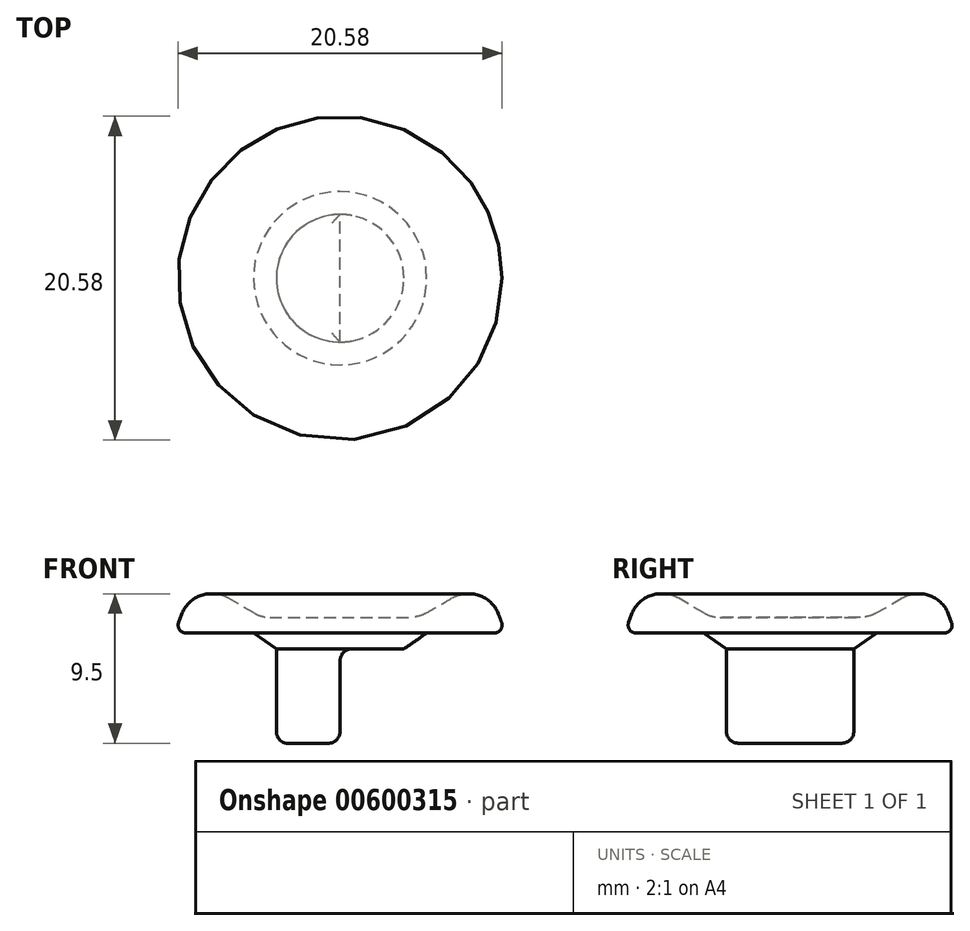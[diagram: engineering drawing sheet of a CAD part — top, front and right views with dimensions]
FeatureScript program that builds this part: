
annotation { "Feature Type Name" : "Feature", "Feature Type Description" : "" }
export const myFeature = defineFeature(function(context is Context, id is Id, definition is map)
    precondition{}
    {
        {
            var Q0;
            Q0=qCreatedBy(makeId("Front.planeOp"),FACE);
            var sketch = newSketch(context, id + "F0", { "sketchPlane" : qUnion([Q0])});
            skLineSegment(sketch, "E0", {"start": v(4.05, 6) * mm, "end": v(5.5, 7) * mm});
            skLineSegment(sketch, "E1", {"start": v(5.5, 7) * mm, "end": v(10.5, 7) * mm});
            skLineSegment(sketch, "E2", {"start": v(0, 8) * mm, "end": v(0, 0) * mm});
            skLineSegment(sketch, "E3", {"start": v(4.05, 6) * mm, "end": v(4.05, 0) * mm});
            skLineSegment(sketch, "E4", {"start": v(4.05, 0) * mm, "end": v(0, 0) * mm});
            skPoint(sketch, "E5.orphan", {"position": v(0, 0) * mm});
            skLineSegment(sketch, "E6", {"start": v(10.5, 7) * mm, "end": v(9.6, 9.5) * mm});
            skLineSegment(sketch, "E7", {"start": v(9.6, 9.5) * mm, "end": v(7.6, 9.5) * mm});
            skLineSegment(sketch, "E8", {"start": v(7.6, 9.5) * mm, "end": v(5, 8) * mm});
            skLineSegment(sketch, "E9", {"start": v(5, 8) * mm, "end": v(0, 8) * mm});
            skSolve(sketch);
        }
        {
            var Q0;
            Q0=qSketchRegion(id+"F0",true);
            var Q1;
            Q1=sQuery(id+"F0.wireOp",EDGE,"E2");
            revolve(context, id + "F1", {"entities" : qUnion([Q0]), "axis" : qUnion([Q1]), "revolveType" : RevolveType.FULL});
        }
        {
            var Q0;
            Q0=makeQuery(id+"F1.opRevolve","SWEPT_FACE",FACE,{"disambiguationData":[OSD([sQuery(id+"F0.wireOp",EDGE,"E4")])]});
            var sketch = newSketch(context, id + "F2", { "sketchPlane" : qUnion([Q0])});
            skLineSegment(sketch, "E10.bottom", {"start": v(0, 4.05) * mm, "end": v(4.05, 4.05) * mm});
            skLineSegment(sketch, "E10.top", {"start": v(0, -4.05) * mm, "end": v(4.05, -4.05) * mm});
            skLineSegment(sketch, "E10.left", {"start": v(0, 4.05) * mm, "end": v(0, -4.05) * mm});
            skLineSegment(sketch, "E10.right", {"start": v(4.05, 4.05) * mm, "end": v(4.05, -4.05) * mm});
            skSolve(sketch);
        }
        {
            var Q0;
            Q0 = qSketchRegion(id + "F2", true);
            extrude(context, id + "F3", {"entities" : qUnion([Q0]), "operationType" : NewBodyOperationType.REMOVE, "oppositeDirection" : true, "depth" : 6 * mm, "offsetDistance" : 25 * mm});
        }
        {
            var Q0;
            {var subQ2=makeQuery(id+"F2R5GIXbNTLPHZD_2.boolean.opBoolean","COPY",FACE,{"derivedFrom":makeQuery(id+"F2R5GIXbNTLPHZD_2.opExtrude","SWEPT_FACE",FACE,{"disambiguationData":[OSD([sQuery(id+"F2.wireOp",EDGE,"6RF5FfAt-YfcN-XYpJ-voTT-JPPEjn318RsV")])]})});Q0=makeQuery(id+"Fmqv6moUgZnORJw_2.2.F2R5GIXbNTLPHZD_2.boolean.opBoolean","SPLIT",FACE,{"disambiguationData":[TD([subQ2])],"derivedFrom":makeQuery(id+"Fmqv6moUgZnORJw_2.1.F2R5GIXbNTLPHZD_2.boolean.opBoolean","SPLIT",FACE,{"disambiguationData":[TD([subQ2])],"derivedFrom":makeQuery(id+"F1.opRevolve","SWEPT_FACE",FACE,{"disambiguationData":[OSD([sQuery(id+"F0.wireOp",EDGE,"E4")])]})})});}
            var Q1;
            {var subQ1=makeQuery(id+"Fmqv6moUgZnORJw_2.1.F2R5GIXbNTLPHZD_2.opExtrude","SWEPT_FACE",FACE,{"disambiguationData":[OSD([sQuery(id+"F2.wireOp",EDGE,"kqsyaNb8-ErKI-FfWI-nr5y-aiWRytRq8sQ2")])]});var subQ3=sQuery(id+"F2.wireOp",EDGE,"6RF5FfAt-YfcN-XYpJ-voTT-JPPEjn318RsV");Q1=makeQuery(id+"Fmqv6moUgZnORJw_2.2.F2R5GIXbNTLPHZD_2.boolean.opBoolean","SPLIT",FACE,{"disambiguationData":[TD([makeQuery(id+"Fmqv6moUgZnORJw_2.1.F2R5GIXbNTLPHZD_2.boolean.opBoolean","COPY",FACE,{"derivedFrom":subQ1})])],"derivedFrom":makeQuery(id+"Fmqv6moUgZnORJw_2.1.F2R5GIXbNTLPHZD_2.boolean.opBoolean","SPLIT",FACE,{"disambiguationData":[TD([makeQuery(id+"F2R5GIXbNTLPHZD_2.boolean.opBoolean","COPY",FACE,{"derivedFrom":makeQuery(id+"F2R5GIXbNTLPHZD_2.opExtrude","SWEPT_FACE",FACE,{"disambiguationData":[OSD([subQ3])]})})])],"derivedFrom":makeQuery(id+"F1.opRevolve","SWEPT_FACE",FACE,{"disambiguationData":[OSD([sQuery(id+"F0.wireOp",EDGE,"E4")])]})})});}
            var Q2;
            Q2=makeQuery(id+"Fmqv6moUgZnORJw_2.1.F2R5GIXbNTLPHZD_2.boolean.opBoolean","SPLIT",FACE,{"disambiguationData":[TD([makeQuery(id+"F2R5GIXbNTLPHZD_2.boolean.opBoolean","COPY",FACE,{"derivedFrom":makeQuery(id+"F2R5GIXbNTLPHZD_2.opExtrude","SWEPT_FACE",FACE,{"disambiguationData":[OSD([sQuery(id+"F2.wireOp",EDGE,"kqsyaNb8-ErKI-FfWI-nr5y-aiWRytRq8sQ2")])]})})])],"derivedFrom":makeQuery(id+"F1.opRevolve","SWEPT_FACE",FACE,{"disambiguationData":[OSD([sQuery(id+"F0.wireOp",EDGE,"E4")])]})});
            var Q3;
            Q3=makeQuery(id+"F3.boolean.opBoolean","COPY",EDGE,{"derivedFrom":makeQuery(id+"F3.opExtrude","CAP_EDGE",EDGE,{"disambiguationData":[OSD([sQuery(id+"F2.wireOp",EDGE,"E10.left")])],"isStart":false})});
            fillet(context, id + "F4", {"entities" : qUnion([Q0, Q1, Q2, Q3]), "radius" : .75 * mm, "tangentPropagation" : true, "allowEdgeOverflow" : false});
        }
        {
            var Q0;
            Q0=makeQuery(id+"F1.opRevolve","SWEPT_FACE",FACE,{"disambiguationData":[OSD([sQuery(id+"F0.wireOp",EDGE,"E7")])]});
            var Q1;
            Q1=makeQuery(id+"F1.opRevolve","SWEPT_EDGE",EDGE,{"disambiguationData":[OSD([sQuery(id+"F0.wireOp",EDGE,"E8"),sQuery(id+"F0.wireOp",EDGE,"E9")])]});
            fillet(context, id + "F5", {"entities" : qUnion([Q0, Q1]), "radius" : 2 * mm, "tangentPropagation" : true, "allowEdgeOverflow" : false});
        }
        {
            var Q0;
            Q0=makeQuery(id+"F1.opRevolve","SWEPT_EDGE",EDGE,{"disambiguationData":[OSD([sQuery(id+"F0.wireOp",EDGE,"E1"),sQuery(id+"F0.wireOp",EDGE,"E6")])]});
            fillet(context, id + "F6", {"entities" : qUnion([Q0]), "radius" : .5 * mm, "tangentPropagation" : true, "allowEdgeOverflow" : false});
        }
    });
